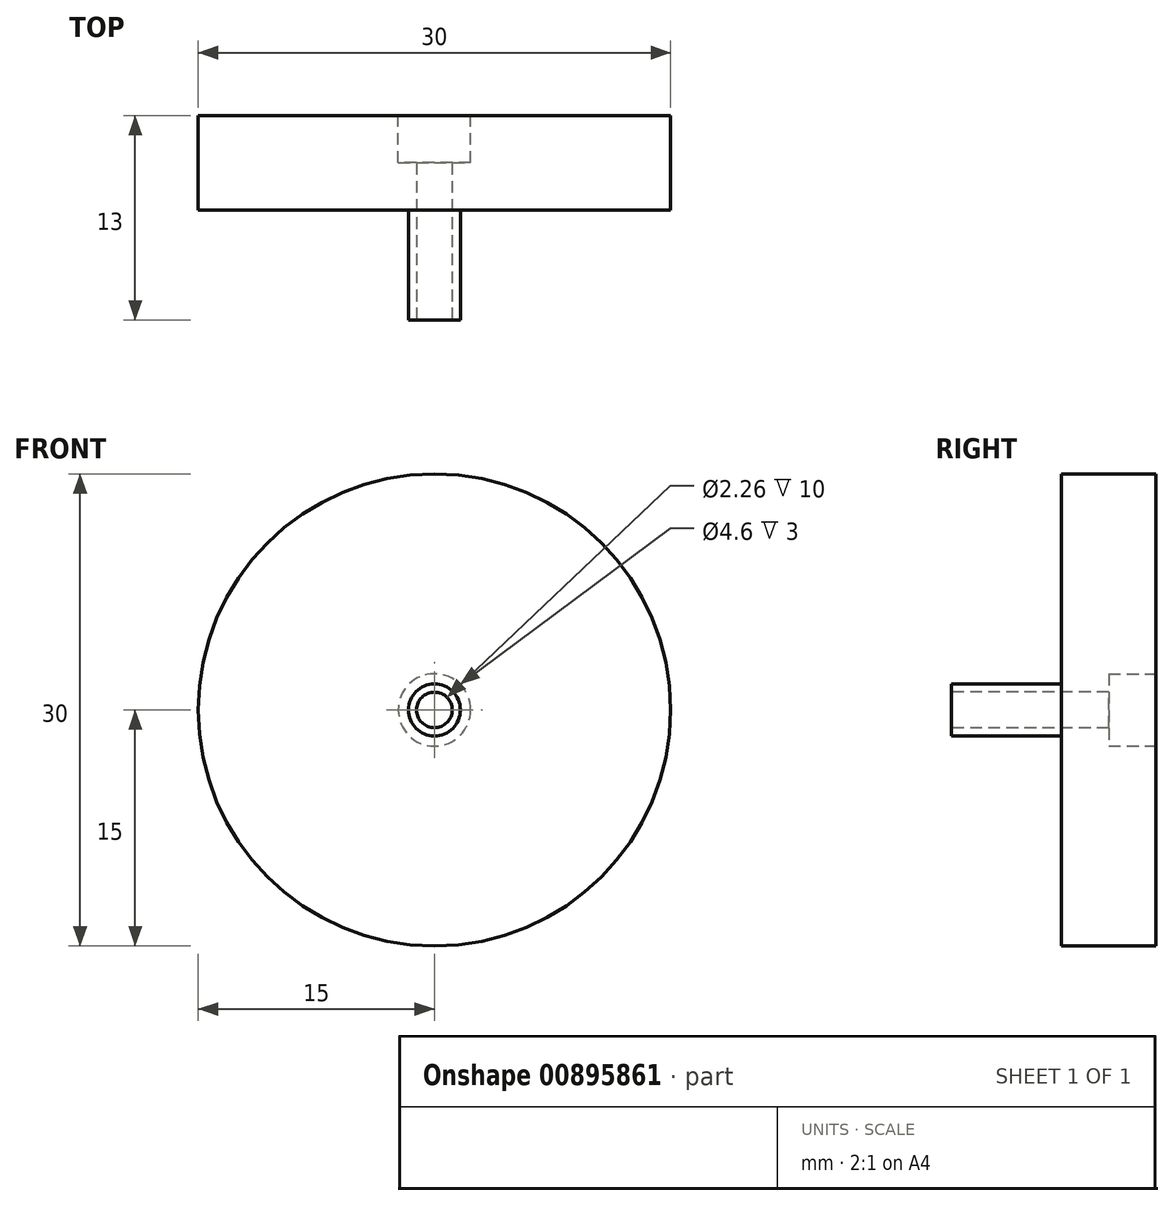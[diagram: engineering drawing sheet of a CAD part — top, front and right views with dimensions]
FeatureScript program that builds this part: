
annotation { "Feature Type Name" : "Feature", "Feature Type Description" : "" }
export const myFeature = defineFeature(function(context is Context, id is Id, definition is map)
    precondition{}
    {
        {
            var Q0;
            Q0=qCreatedBy(makeId("Front.planeOp"),FACE);
            var sketch = newSketch(context, id + "F0", { "sketchPlane" : qUnion([Q0])});
            skCircle(sketch, "E0", {"center": v(0, 0) * mm, "radius": 15 * mm});
            skCircle(sketch, "E1", {"center": v(0, 0) * mm, "radius": 2.3 * mm});
            skCircle(sketch, "E2", {"center": v(0, 0) * mm, "radius": 1.65 * mm});
            skCircle(sketch, "E3", {"center": v(0, 0) * mm, "radius": 1.13 * mm});
            skSolve(sketch);
        }
        {
            var Q0;
            Q0=makeQuery(id+"F0.imprint","IMPRINT",FACE,{"disambiguationData":[TD([[makeQuery(id+"F0.imprint","IMPRINT",EDGE,{"derivedFrom":sQuery(id+"F0.wireOp",EDGE,"E0")}),1.0]])]});
            var Q1;
            Q1=makeQuery(id+"F0.imprint","IMPRINT",FACE,{"disambiguationData":[TD([[makeQuery(id+"F0.imprint","IMPRINT",EDGE,{"derivedFrom":sQuery(id+"F0.wireOp",EDGE,"E1")}),1.0]])]});
            var Q2;
            Q2=makeQuery(id+"F0.imprint","IMPRINT",FACE,{"disambiguationData":[TD([[makeQuery(id+"F0.imprint","IMPRINT",EDGE,{"derivedFrom":sQuery(id+"F0.wireOp",EDGE,"E2")}),1.0]])]});
            extrude(context, id + "F1", {"entities" : qUnion([Q0, Q1, Q2]), "oppositeDirection" : true, "depth" : 6 * mm, "offsetDistance" : 25 * mm});
        }
        {
            var Q0;
            Q0=makeQuery(id+"F0.imprint","IMPRINT",FACE,{"disambiguationData":[TD([[makeQuery(id+"F0.imprint","IMPRINT",EDGE,{"derivedFrom":sQuery(id+"F0.wireOp",EDGE,"E2")}),1.0]])]});
            extrude(context, id + "F2", {"entities" : qUnion([Q0]), "operationType" : NewBodyOperationType.ADD, "depth" : 7 * mm, "offsetDistance" : 25 * mm});
        }
        {
            var Q0;
            Q0=makeQuery(id+"F1.opExtrude","CAP_FACE",FACE,{"disambiguationData":[OSD([sQuery(id+"F0.wireOp",EDGE,"E0"),sQuery(id+"F0.wireOp",EDGE,"E3")])],"isStart":false});
            var sketch = newSketch(context, id + "F3", { "sketchPlane" : qUnion([Q0])});
            skCircle(sketch, "E4", {"center": v(0, 0) * mm, "radius": 2.3 * mm});
            skSolve(sketch);
        }
        {
            var Q0;
            Q0=makeQuery(id+"F3.imprint","IMPRINT",FACE,{"disambiguationData":[TD([[makeQuery(id+"F3.imprint","IMPRINT",EDGE,{"derivedFrom":sQuery(id+"F3.wireOp",EDGE,"E4")}),1.0]])]});
            extrude(context, id + "F4", {"entities" : qUnion([Q0]), "operationType" : NewBodyOperationType.REMOVE, "oppositeDirection" : true, "depth" : 3 * mm, "offsetDistance" : 25 * mm});
        }
    });
